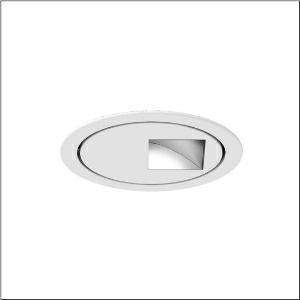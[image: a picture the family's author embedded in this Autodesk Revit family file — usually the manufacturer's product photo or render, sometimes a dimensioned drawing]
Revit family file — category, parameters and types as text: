
# Revit family: lunis_11_mini_round_51dk11cd2wn21
name_source: partatom
category: Lighting Fixtures
units: mm (PartAtom-declared; Revit-internal decimal feet)

## family parameters
Cut with Voids When Loaded = No
Host = Face
Light Source = No
Part Type = Normal
Room Calculation Point = No
Round Connector Dimension = Use Diameter
Shared = No

## types (1)
- Lunis 11 mini round (1 x LED 4000K / CRI = 90 (unbekannt), 2120 lm, 4000K)
    Apparent Load = 28 VA
    CIE Flux Codes = 44 77 97 100 100
    Color Rendering = 90
    Color Temperature = 4000K
    Default Elevation = 1800 mm
    Description = Lunis 11 mini round, downlight, light control with wallwasher, of highly reflective aluminium, highly specular, light emission: direct distribution, LED rated luminous flux: 2.120lm, light colour: 940, control gear: ECG, with terminal, 5-pole, mains connection: 220..230V, AC/DC, 0/50..60Hz, LED module, luminaire module, of aluminium, highly specular, white, diameter: 176mm, clamping range: 1..40mm, recessing ring, of plastic, traffic white (RAL 9016), protection rating (complete): IP20, insulation class (complete): insulation class II (safety insulation), certification: CE, permissible ambient temperature for indoor applications: 0..+35°C, packaging unit: 1 piece
    Height = 0 mm  [stored 0 ft]
    Lamp = 1 x LED 4000K / CRI >= 90 (unbekannt)
    Lamp Light Flux = 2120 lm
    Lamp count = 1
    Length = 176 mm
    Luminous efficacy = 76 lm/W
    Manufacturer = Siteco
    ModVariant = No
    Model = 51DK11CD2WN21
    Mounting Place = Ceiling
    Mounting Type = Recessed
    Number of Poles = 1
    OnlyDefault = Yes
    Power Factor = 1
    Product Name = Lunis 11 mini round
    Product group = downlight
    ProductGroupID = 400
    Protection Class = Protection class II
    Protection Degree = IP 20
    RLX_Detail_Level = 1
    RLX_Emergency_Light_Flux = 0 lm
    RLX_Emergency_Type = 0
    RLX_Emergency_Type_DB = No
    RlxData = <blob elided: 59365 chars, md5=841b35d8>
    Socket = socket
    Standby Power = 0 W
    System Light Flux = 2120 lm
    System Power = 28 W
    Type Comments = Product without accessories
    Type Image = l_1004772.jpg
    URL = http://relux.com
    VarID = ---
    Voltage = 0 V
    Weight = 0.00 kg
    Width = 176 mm

note: [stored X ft] marks values corroborated as IEEE doubles in the binary element streams (Revit-internal decimal feet)

## geometry (parser evidence)
native form markers: Blend x4, Sweep x11
no freeform markers — native parametric forms only
